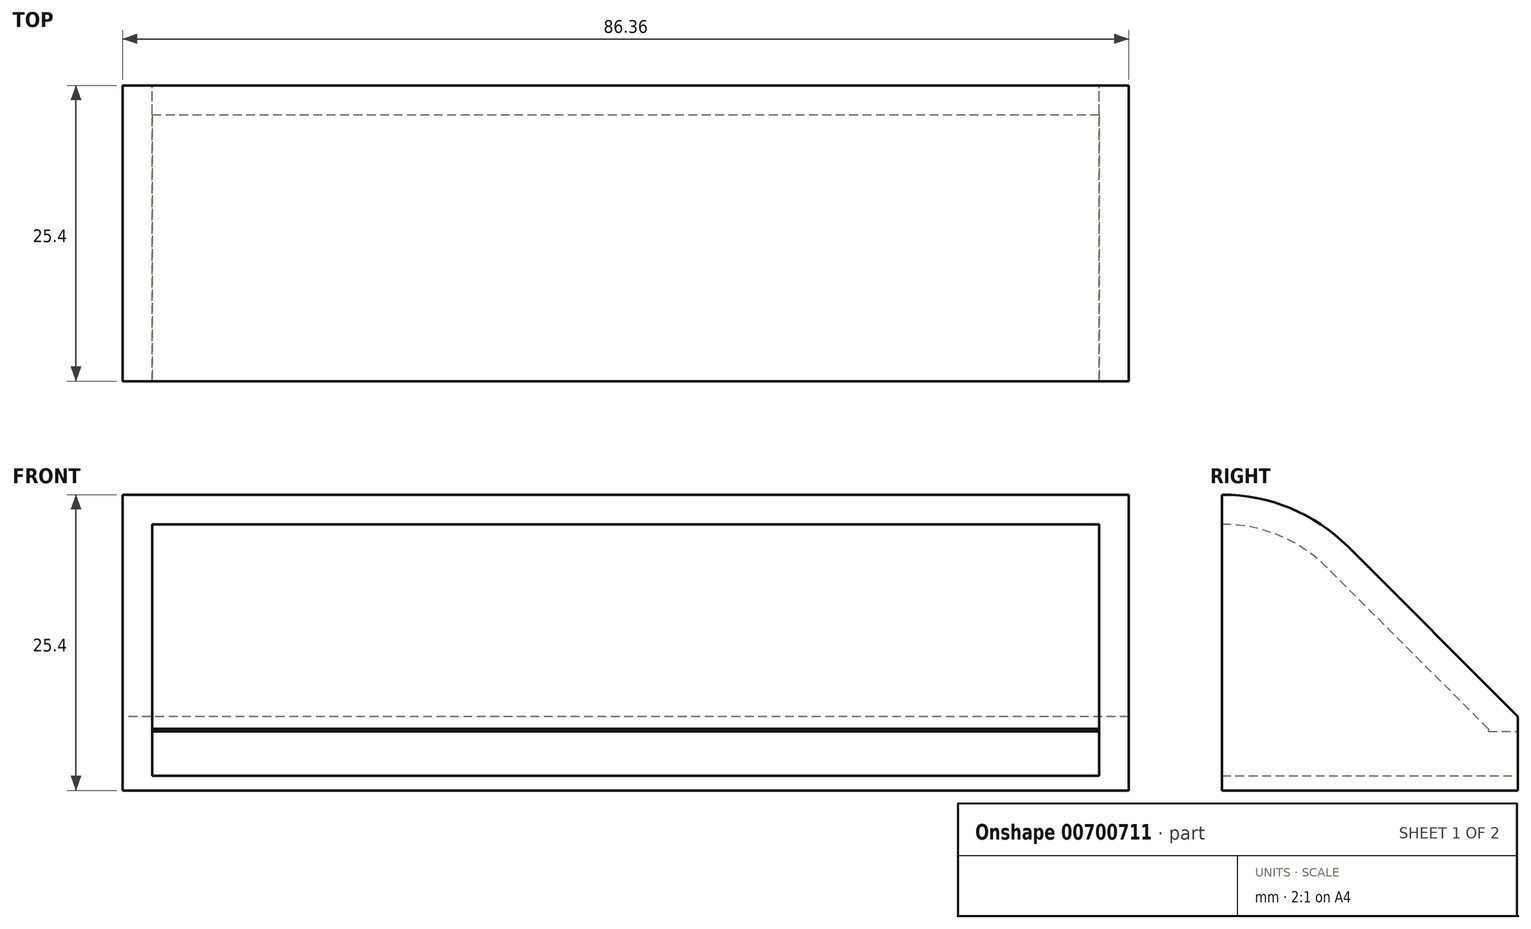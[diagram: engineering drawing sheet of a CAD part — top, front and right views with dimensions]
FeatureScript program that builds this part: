
annotation { "Feature Type Name" : "Feature", "Feature Type Description" : "" }
export const myFeature = defineFeature(function(context is Context, id is Id, definition is map)
    precondition{}
    {
        {
            var Q0;
            Q0=qCreatedBy(makeId("Front.planeOp"),FACE);
            var sketch = newSketch(context, id + "F0", { "sketchPlane" : qUnion([Q0])});
            skLineSegment(sketch, "E0.bottom", {"start": v(43.18, 3.18) * mm, "end": v(-43.18, 3.18) * mm});
            skLineSegment(sketch, "E0.top", {"start": v(43.18, -3.18) * mm, "end": v(-43.18, -3.18) * mm});
            skLineSegment(sketch, "E0.left", {"start": v(43.18, 3.18) * mm, "end": v(43.18, -3.18) * mm});
            skLineSegment(sketch, "E0.right", {"start": v(-43.18, 3.18) * mm, "end": v(-43.18, -3.18) * mm});
            skPoint(sketch, "E0.middle", {"position": v(0, 0) * mm});
            skSolve(sketch);
        }
        {
            var Q0;
            Q0=makeQuery(id+"F0.imprint","IMPRINT",FACE,{"disambiguationData":[TD([[makeQuery(id+"F0.imprint","IMPRINT",EDGE,{"derivedFrom":sQuery(id+"F0.wireOp",EDGE,"E0.bottom")}),1.0]])]});
            extrude(context, id + "F1", {"entities" : qUnion([Q0]), "depth" : 19.05 * mm, "offsetDistance" : 25.4 * mm});
        }
        {
            var Q0;
            Q0=makeQuery(id+"F1.opExtrude","CAP_FACE",FACE,{"disambiguationData":[OSD([sQuery(id+"F0.wireOp",EDGE,"E0.bottom"),sQuery(id+"F0.wireOp",EDGE,"E0.top"),sQuery(id+"F0.wireOp",EDGE,"E0.left"),sQuery(id+"F0.wireOp",EDGE,"E0.right")])],"isStart":false});
            var sketch = newSketch(context, id + "F2", { "sketchPlane" : qUnion([Q0])});
            skLineSegment(sketch, "E1.bottom", {"start": v(-43.18, -3.18) * mm, "end": v(43.18, -3.18) * mm});
            skLineSegment(sketch, "E1.top", {"start": v(-43.18, 22.22) * mm, "end": v(43.18, 22.22) * mm});
            skLineSegment(sketch, "E1.left", {"start": v(-43.18, -3.18) * mm, "end": v(-43.18, 22.22) * mm});
            skLineSegment(sketch, "E1.right", {"start": v(43.18, -3.18) * mm, "end": v(43.18, 22.22) * mm});
            skSolve(sketch);
        }
        {
            var Q0;
            {var subQ0=sQuery(id+"F2.wireOp",EDGE,"E1.top");Q0=makeQuery(id+"F2.imprint","IMPRINT",FACE,{"disambiguationData":[TD([[makeQuery(id+"F2.imprint","IMPRINT",EDGE,{"derivedFrom":subQ0}),-1.0]])]});}
            var Q1;
            {var subQ0=sQuery(id+"F2.wireOp",EDGE,"E1.bottom");Q1=makeQuery(id+"F2.imprint","IMPRINT",FACE,{"disambiguationData":[TD([[makeQuery(id+"F2.imprint","IMPRINT",EDGE,{"derivedFrom":subQ0}),-1.0]])]});}
            extrude(context, id + "F3", {"entities" : qUnion([Q0, Q1]), "operationType" : NewBodyOperationType.ADD, "depth" : 6.35 * mm, "offsetDistance" : 25.4 * mm});
        }
        {
            var Q1;
            Q1=makeQuery(id+"F1.opExtrude","SWEPT_FACE",FACE,{"disambiguationData":[OSD([sQuery(id+"F0.wireOp",EDGE,"E0.bottom")])]});
            var Q2;
            Q2=makeQuery(id+"F3.opExtrude","SWEPT_FACE",FACE,{"disambiguationData":[OSD([sQuery(id+"F2.wireOp",EDGE,"E1.top")])]});
            loft(context, id + "F4", {"operationType" : NewBodyOperationType.ADD, "sheetProfilesArray" : [{ "sheetProfileEntities" : qUnion([Q1]) }, { "sheetProfileEntities" : qUnion([Q2]) }]});
        }
        {
            var Q0;
            {var subQ0=sQuery(id+"F2.wireOp",EDGE,"E1.top");var subQ1=makeQuery(id+"F3.opExtrude","CAP_EDGE",EDGE,{"disambiguationData":[OSD([subQ0])],"isStart":true});var subQ2=sQuery(id+"F2.wireOp",EDGE,"E1.right");var subQ3=sQuery(id+"F2.wireOp",EDGE,"E1.left");Q0=makeQuery(id+"F4.boolean.opBoolean","MERGE",EDGE,{"derivedFrom":[subQ1,makeQuery(id+"F4.opLoft","MID_CAP_EDGE",EDGE,{"disambiguationData":[OSD([subQ0,subQ3,subQ2]),TDD([makeQuery(id+"F3.opExtrude","CAP_VERTEX",VERTEX,{"disambiguationData":[OSD([subQ0,subQ3])],"isStart":true}),makeQuery(id+"F3.opExtrude","CAP_VERTEX",VERTEX,{"disambiguationData":[OSD([subQ0,subQ2])],"isStart":true}),subQ1])],"capPos":1.0})]});}
            fillet(context, id + "F5", {"entities" : qUnion([Q0]), "radius" : 15.24 * mm, "tangentPropagation" : true, "allowEdgeOverflow" : false});
        }
        {
            var Q0;
            Q0=makeQuery(id+"F3.opExtrude","CAP_FACE",FACE,{"disambiguationData":[OSD([sQuery(id+"F2.wireOp",EDGE,"E1.bottom"),sQuery(id+"F2.wireOp",EDGE,"E1.top"),sQuery(id+"F2.wireOp",EDGE,"E1.left"),sQuery(id+"F2.wireOp",EDGE,"E1.right")])],"isStart":false});
            shell(context, id + "F6", {"entities" : qUnion([Q0]), "thickness" : 2.54 * mm});
        }
        {
            var Q0;
            Q0=makeQuery(id+"F1.opExtrude","CAP_FACE",FACE,{"disambiguationData":[OSD([sQuery(id+"F0.wireOp",EDGE,"E0.bottom"),sQuery(id+"F0.wireOp",EDGE,"E0.top"),sQuery(id+"F0.wireOp",EDGE,"E0.left"),sQuery(id+"F0.wireOp",EDGE,"E0.right")])],"isStart":true});
            var sketch = newSketch(context, id + "F7", { "sketchPlane" : qUnion([Q0])});
            skLineSegment(sketch, "E2.bottom", {"start": v(40.64, 1.9) * mm, "end": v(-40.64, 1.9) * mm});
            skLineSegment(sketch, "E2.top", {"start": v(40.64, -1.9) * mm, "end": v(-40.64, -1.9) * mm});
            skLineSegment(sketch, "E2.left", {"start": v(40.64, 1.9) * mm, "end": v(40.64, -1.9) * mm});
            skLineSegment(sketch, "E2.right", {"start": v(-40.64, 1.9) * mm, "end": v(-40.64, -1.9) * mm});
            skPoint(sketch, "E2.middle", {"position": v(0, 0) * mm});
            skSolve(sketch);
        }
        {
            var Q0;
            Q0=makeQuery(id+"F7.imprint","IMPRINT",FACE,{"disambiguationData":[TD([[makeQuery(id+"F7.imprint","IMPRINT",EDGE,{"derivedFrom":sQuery(id+"F7.wireOp",EDGE,"E2.bottom")}),1.0]])]});
            extrude(context, id + "F8", {"entities" : qUnion([Q0]), "operationType" : NewBodyOperationType.REMOVE, "endBound" : BoundingType.THROUGH_ALL, "oppositeDirection" : true, "depth" : 25.4 * mm, "offsetDistance" : 25.4 * mm});
        }
    });
